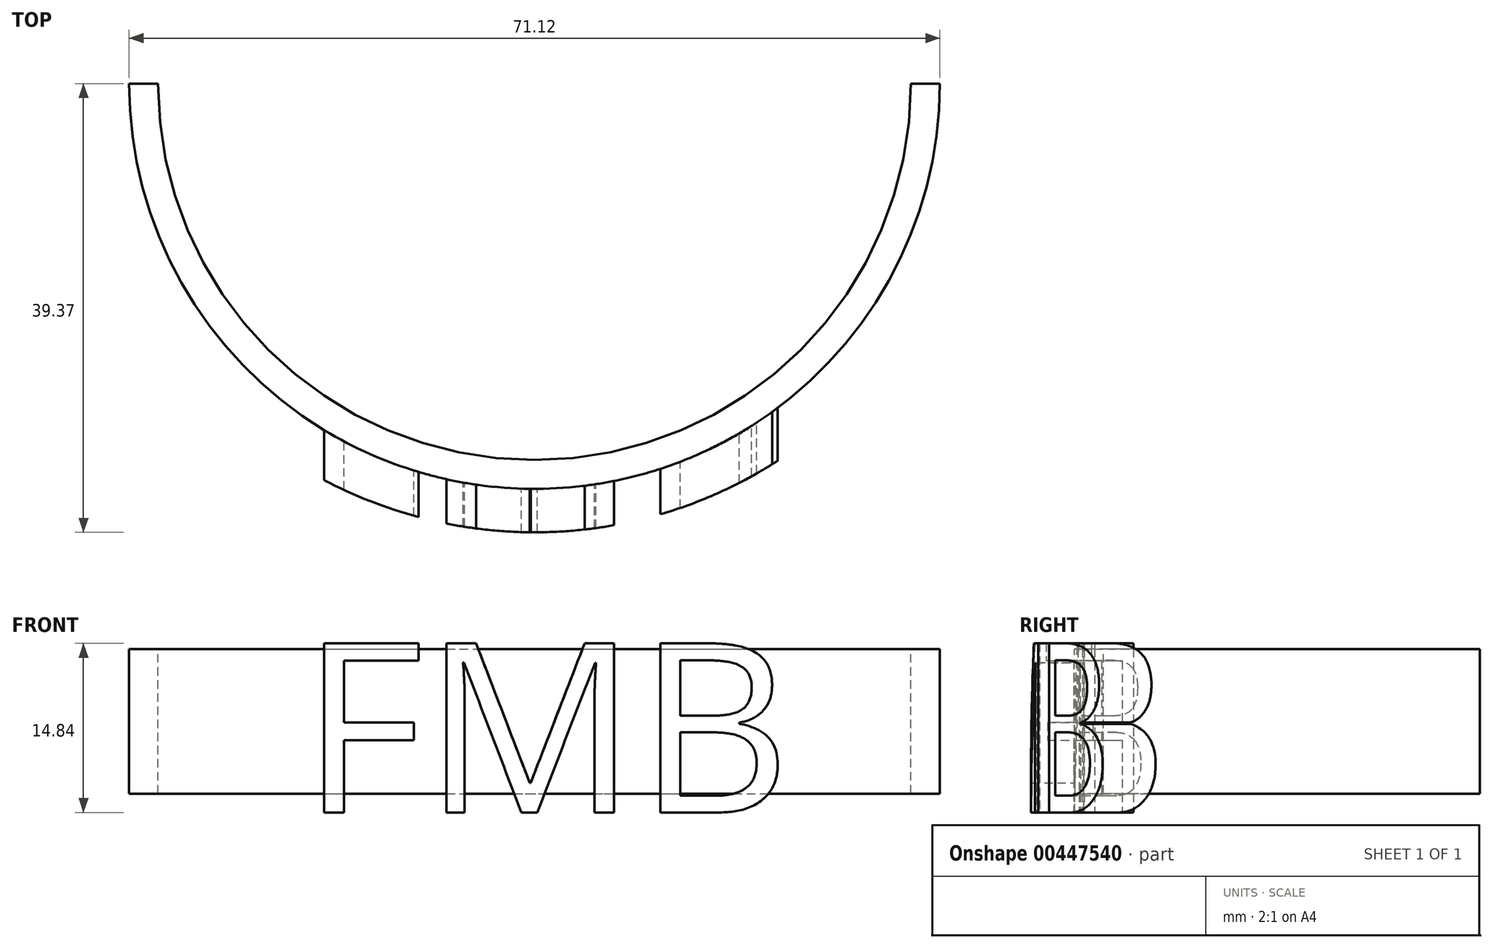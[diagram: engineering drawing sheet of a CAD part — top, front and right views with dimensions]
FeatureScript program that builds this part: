
annotation { "Feature Type Name" : "Feature", "Feature Type Description" : "" }
export const myFeature = defineFeature(function(context is Context, id is Id, definition is map)
    precondition{}
    {
        {
            var Q0;
            Q0=qCreatedBy(makeId("Front.planeOp"),FACE);
            var sketch = newSketch(context, id + "F0", { "sketchPlane" : qUnion([Q0])});
            skLineSegment(sketch, "E0", {"start": v(-5.2, 0.62) * mm, "end": v(37.97, 0.62) * mm, "construction": true});
            skText(sketch, "E1", { "text": "FMB", "fontName": "OpenSans-Regular.ttf"});
            const initialGuessF0  = {"E1": [-0.0052, -0.01435, 1, 0, 0.01497]};
            skSetInitialGuess(sketch, initialGuessF0);
            skSolve(sketch);
        }
        {
            var Q0;
            Q0 = qSketchRegion(id + "F0", true);
            extrude(context, id + "F1", {"entities" : qUnion([Q0]), "depth" : 32.5 * mm});
        }
        {
            var Q0;
            Q0=qCreatedBy(makeId("Top.planeOp"),FACE);
            var sketch = newSketch(context, id + "F2", { "sketchPlane" : qUnion([Q0])});
            skLineSegment(sketch, "E2.0", {"start": v(35.6, -32.51) * mm, "end": v(35.6, 0) * mm, "construction": true});
            skLineSegment(sketch, "E3.0", {"start": v(-5.53, -32.51) * mm, "end": v(-5.53, 0) * mm, "construction": true});
            skLineSegment(sketch, "E4", {"start": v(35.6, 0) * mm, "end": v(15.29, 0) * mm, "construction": true});
            skLineSegment(sketch, "E5", {"start": v(15.29, 0) * mm, "end": v(15.29, 12.7) * mm, "construction": true});
            skLineSegment(sketch, "E6", {"start": v(15.29, 12.7) * mm, "end": v(-16.2, 12.7) * mm, "construction": true});
            skLineSegment(sketch, "E7", {"start": v(15.29, 12.7) * mm, "end": v(37.87, 12.7) * mm, "construction": true});
            skArc(sketch, "E8", {"start": v(-20.27, 12.7) * mm, "mid": v(15.29, -22.86) * mm, "end": v(50.85, 12.7) * mm});
            skArc(sketch, "E9", {"start": v(54.66, 12.7) * mm, "mid": v(15.29, -26.67) * mm, "end": v(-24.08, 12.7) * mm});
            skLineSegment(sketch, "E10", {"start": v(-20.27, 12.7) * mm, "end": v(-24.08, 12.7) * mm});
            skLineSegment(sketch, "E11", {"start": v(50.85, 12.7) * mm, "end": v(54.66, 12.7) * mm});
            skSolve(sketch);
        }
        {
            var Q0;
            Q0 = qSketchRegion(id + "F2", true);
            extrude(context, id + "F3", {"entities" : qUnion([Q0]), "operationType" : NewBodyOperationType.INTERSECT, "depth" : 12.2 * mm, "hasSecondDirection" : true, "secondDirectionOppositeDirection" : true, "secondDirectionDepth" : 22.86 * mm});
        }
        {
            var Q0;
            Q0=qCreatedBy(makeId("Top.planeOp"),FACE);
            var sketch = newSketch(context, id + "F4", { "sketchPlane" : qUnion([Q0])});
            skPoint(sketch, "E12.0", {"position": v(50.85, 12.7) * mm});
            skPoint(sketch, "E13.0", {"position": v(15.29, 12.7) * mm});
            skPoint(sketch, "E14.0", {"position": v(-20.27, 12.7) * mm});
            skLineSegment(sketch, "E15", {"start": v(50.85, 12.7) * mm, "end": v(48.3, 12.7) * mm});
            skArc(sketch, "E16", {"start": v(50.85, 12.7) * mm, "mid": v(15.29, -22.86) * mm, "end": v(-20.27, 12.7) * mm});
            skArc(sketch, "E17", {"start": v(48.3, 12.7) * mm, "mid": v(15.29, -20.32) * mm, "end": v(-17.73, 12.7) * mm});
            skLineSegment(sketch, "E18", {"start": v(-17.73, 12.7) * mm, "end": v(-20.27, 12.7) * mm});
            skSolve(sketch);
        }
        {
            var Q0;
            Q0 = qSketchRegion(id + "F4", true);
            extrude(context, id + "F5", {"entities" : qUnion([Q0]), "operationType" : NewBodyOperationType.ADD, "oppositeDirection" : true, "depth" : 12.7 * mm});
        }
    });
